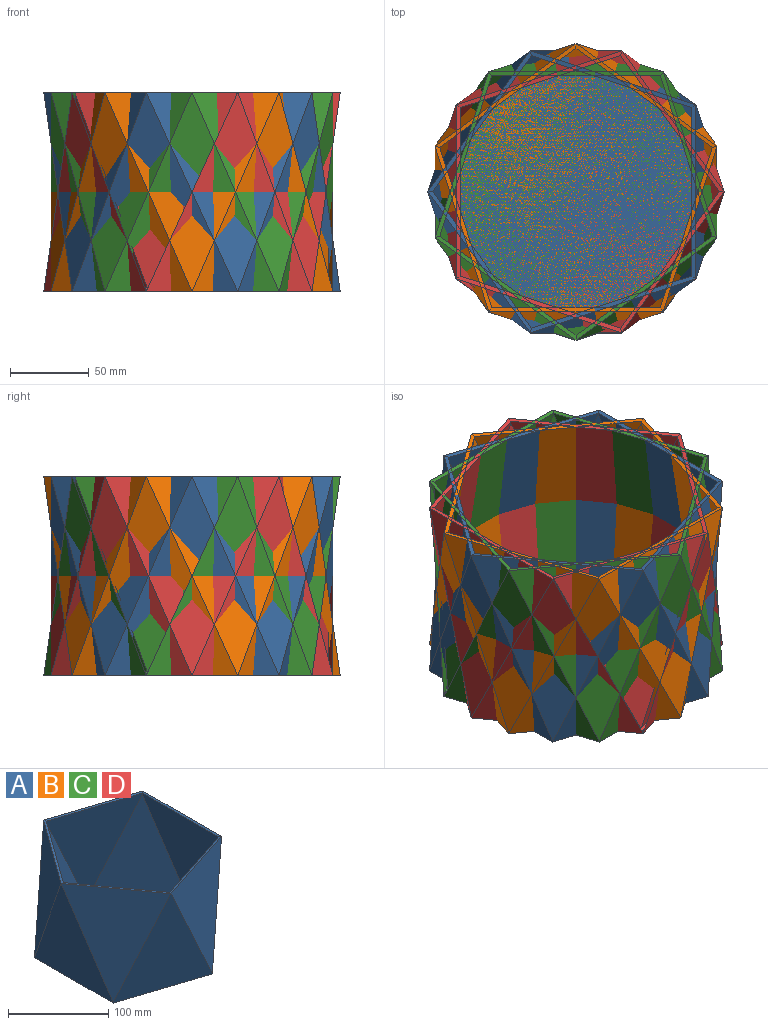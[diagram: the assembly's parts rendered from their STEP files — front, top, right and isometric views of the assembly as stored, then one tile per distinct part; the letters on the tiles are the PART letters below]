
ASSEMBLY  parts=4 mates=3
PART A: 30 faces, bbox 188.6x179.4x127 mm
  f0: plane 124.1x87mm, normal (0.8,-0.58,-0.14), area 6858.2mm2, adj f1,f2,f5,f20,f28,f29
  f1: plane 174.01x165.49mm, normal (0,0,1), area 19946.1mm2, adj f0,f2,f5,f9,f12,f13,f15,f17
  f2: plane 124.1x102.28mm, normal (-0.31,-0.94,-0.14), area 6858.2mm2, adj f0,f1,f7,f9,f17,f28
  f3: plane 179.4x170.62mm, normal (0,0,-1), area 21151.3mm2, adj f8,f10,f11,f19,f27
  f4: plane 127x89.7mm, normal (-0.8,0.58,0.14), area 7111.2mm2, adj f19,f27,f29
  f5: plane 124.1x87mm, normal (0.8,0.58,-0.14), area 6858.2mm2, adj f0,f1,f6,f12,f15,f20
  f6: plane 89.7x66.13mm, normal (0.11,0.08,0.99), area 277mm2, adj f5,f14,f26,f29
  f7: plane 105.45x36.09mm, normal (-0.04,-0.13,0.99), area 277mm2, adj f2,f16,f18,f29
  f8: plane 127x89.7mm, normal (0.8,0.58,-0.14), area 7111.2mm2, adj f3,f16,f24
  f9: plane 122.55x86.56mm, normal (-0.8,-0.58,0.14), area 6621.6mm2, adj f1,f2,f17
  f10: plane 127x89.7mm, normal (0.8,-0.58,-0.14), area 7111.2mm2, adj f3,f24,f25
  f11: plane 127x105.45mm, normal (-0.31,-0.94,-0.14), area 7111.2mm2, adj f3,f25,f26
  f12: plane 124.1x102.28mm, normal (-0.31,0.94,-0.14), area 6858.2mm2, adj f1,f5,f13,f14,f15,f17
  f13: plane 122.55x86.56mm, normal (-0.8,0.58,0.14), area 6621.6mm2, adj f1,f12,f17
  f14: plane 105.45x36.09mm, normal (-0.04,0.13,0.99), area 277mm2, adj f6,f12,f18,f25
  f15: plane 122.55x101.76mm, normal (0.31,0.94,0.14), area 6621.6mm2, adj f1,f5,f12
  f16: plane 127x105.45mm, normal (0.31,0.94,0.14), area 7109.9mm2, adj f7,f8,f21,f22,f23,f27
  f17: plane 124.1x107.54mm, normal (-0.99,0,-0.14), area 6858.2mm2, adj f1,f2,f9,f12,f13,f18
  f18: plane 110.88x2.52mm, normal (-0.14,0,0.99), area 277mm2, adj f7,f14,f17,f24
  f19: plane 127x110.88mm, normal (-0.99,0,-0.14), area 7111.2mm2, adj f3,f4,f26
  f20: plane 122.55x106.99mm, normal (0.99,0,0.14), area 6621.6mm2, adj f0,f1,f5
  f21: plane 2.54x0.5mm, normal (0.81,0.59,0), area 0.8mm2, adj f16,f22,f23
  f22: plane 0.94x0.5mm, normal (0,0,1), area 0.2mm2, adj f16,f21,f23
  f23: plane 2.54x0.58mm, normal (-0.31,0.95,0), area 0.8mm2, adj f16,f21,f22
  f24: plane 127x110.88mm, normal (0.99,0,0.14), area 7111.2mm2, adj f8,f10,f18
  f25: plane 127x105.45mm, normal (0.31,-0.94,0.14), area 7111.2mm2, adj f10,f11,f14
  f26: plane 127x89.7mm, normal (-0.8,-0.58,0.14), area 7111.2mm2, adj f6,f11,f19
  f27: plane 127x105.45mm, normal (-0.31,0.94,-0.14), area 7111.2mm2, adj f3,f4,f16
  f28: plane 122.55x101.76mm, normal (0.31,-0.94,0.14), area 6621.6mm2, adj f0,f1,f2
  f29: plane 89.7x66.13mm, normal (0.11,-0.08,0.99), area 277mm2, adj f0,f4,f6,f7
PART B: same geometry as A
PART C: same geometry as A
PART D: same geometry as A
PLACE A t=(111.8,-43.94,100.8)mm
PLACE B rot(axis=(0,0,-1),90deg) t=(111.8,-43.94,100.8)mm
PLACE C rot(axis=(0,0,1),90deg) t=(111.8,-43.94,100.8)mm
PLACE D rot(axis=(0,0,1),180deg) t=(111.8,-43.94,100.8)mm
MATE fastened B.f1 <-> D.f1  axis (0,0,1) through (111.8,-43.94,103.34)mm
MATE fastened D.f1 <-> A.f1  axis (0,0,1) through (111.8,-43.94,103.34)mm
MATE fastened C.f1 <-> D.f1  axis (0,0,1) through (111.8,-43.94,103.34)mm
